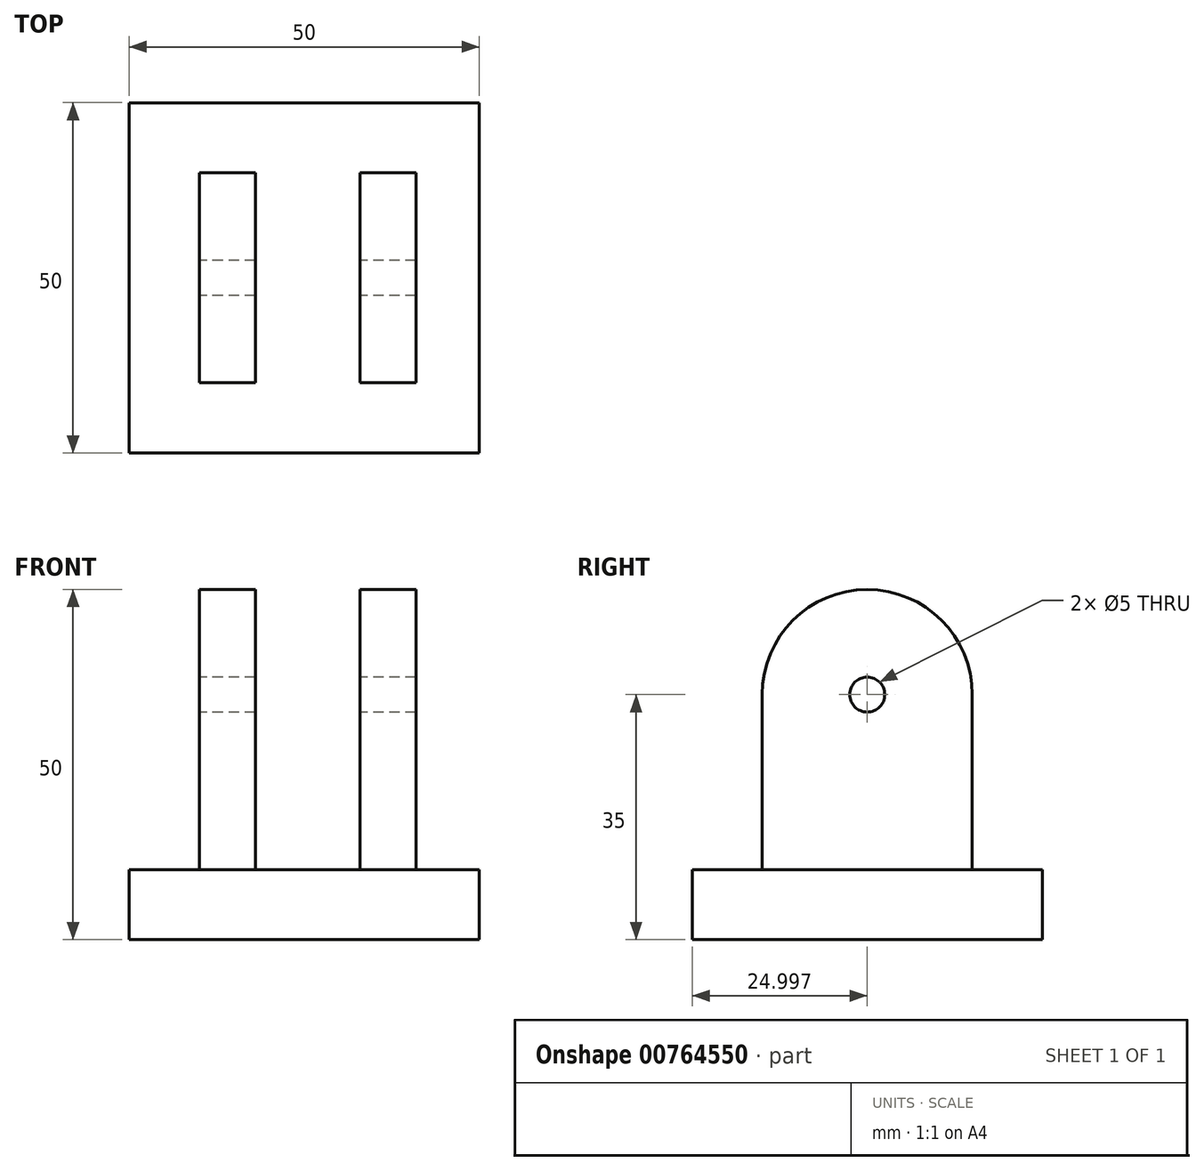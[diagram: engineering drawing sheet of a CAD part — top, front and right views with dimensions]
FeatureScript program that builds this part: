
annotation { "Feature Type Name" : "Feature", "Feature Type Description" : "" }
export const myFeature = defineFeature(function(context is Context, id is Id, definition is map)
    precondition{}
    {
        {
            var Q0;
            Q0=qCreatedBy(makeId("Top.planeOp"),FACE);
            var sketch = newSketch(context, id + "F0", { "sketchPlane" : qUnion([Q0])});
            skLineSegment(sketch, "E0.bottom", {"start": v(-23.15, 24.72) * mm, "end": v(26.85, 24.72) * mm});
            skLineSegment(sketch, "E0.top", {"start": v(-23.15, -25.28) * mm, "end": v(26.85, -25.28) * mm});
            skLineSegment(sketch, "E0.left", {"start": v(-23.15, 24.72) * mm, "end": v(-23.15, -25.28) * mm});
            skLineSegment(sketch, "E0.right", {"start": v(26.85, 24.72) * mm, "end": v(26.85, -25.28) * mm});
            skSolve(sketch);
        }
        {
            var Q0;
            Q0=makeQuery(id+"F0.imprint","IMPRINT",FACE,{"disambiguationData":[TD([[makeQuery(id+"F0.imprint","IMPRINT",EDGE,{"derivedFrom":sQuery(id+"F0.wireOp",EDGE,"E0.bottom")}),-1.0]])]});
            extrude(context, id + "F1", {"entities" : qUnion([Q0]), "depth" : 10 * mm, "offsetDistance" : 25 * mm});
        }
        {
            var Q0;
            Q0=makeQuery(id+"F1.opExtrude","CAP_FACE",FACE,{"disambiguationData":[OSD([sQuery(id+"F0.wireOp",EDGE,"E0.bottom"),sQuery(id+"F0.wireOp",EDGE,"E0.top"),sQuery(id+"F0.wireOp",EDGE,"E0.left"),sQuery(id+"F0.wireOp",EDGE,"E0.right")])],"isStart":false});
            var sketch = newSketch(context, id + "F2", { "sketchPlane" : qUnion([Q0])});
            skLineSegment(sketch, "E1.bottom", {"start": v(-13.15, 14.72) * mm, "end": v(-5.15, 14.72) * mm});
            skLineSegment(sketch, "E1.top", {"start": v(-13.15, -15.28) * mm, "end": v(-5.15, -15.28) * mm});
            skLineSegment(sketch, "E1.left", {"start": v(-13.15, 14.72) * mm, "end": v(-13.15, -15.28) * mm});
            skLineSegment(sketch, "E1.right", {"start": v(-5.15, 14.72) * mm, "end": v(-5.15, -15.28) * mm});
            skSolve(sketch);
        }
        {
            var Q0;
            Q0=makeQuery(id+"F2.imprint","IMPRINT",FACE,{"disambiguationData":[TD([[makeQuery(id+"F2.imprint","IMPRINT",EDGE,{"derivedFrom":sQuery(id+"F2.wireOp",EDGE,"E1.bottom")}),1.0]])]});
            var sketch = newSketch(context, id + "F3", { "sketchPlane" : qUnion([Q0])});
            skLineSegment(sketch, "E2.bottom", {"start": v(9.78, 14.72) * mm, "end": v(17.78, 14.72) * mm});
            skLineSegment(sketch, "E2.top", {"start": v(9.78, -15.28) * mm, "end": v(17.78, -15.28) * mm});
            skLineSegment(sketch, "E2.left", {"start": v(9.78, 14.72) * mm, "end": v(9.78, -15.28) * mm});
            skLineSegment(sketch, "E2.right", {"start": v(17.78, 14.72) * mm, "end": v(17.78, -15.28) * mm});
            skSolve(sketch);
        }
        {
            var Q0;
            Q0=makeQuery(id+"F2.imprint","IMPRINT",FACE,{"disambiguationData":[TD([[makeQuery(id+"F2.imprint","IMPRINT",EDGE,{"derivedFrom":sQuery(id+"F2.wireOp",EDGE,"E1.bottom")}),-1.0]])]});
            extrude(context, id + "F4", {"entities" : qUnion([Q0]), "operationType" : NewBodyOperationType.ADD, "depth" : 40 * mm, "offsetDistance" : 25 * mm});
        }
        {
            var Q0;
            Q0=makeQuery(id+"F3.imprint","IMPRINT",FACE,{"disambiguationData":[TD([[makeQuery(id+"F3.imprint","IMPRINT",EDGE,{"derivedFrom":sQuery(id+"F3.wireOp",EDGE,"E2.bottom")}),-1.0]])]});
            extrude(context, id + "F5", {"entities" : qUnion([Q0]), "operationType" : NewBodyOperationType.ADD, "depth" : 40 * mm, "offsetDistance" : 25 * mm});
        }
        {
            var Q0;
            Q0=makeQuery(id+"F4.opExtrude","CAP_EDGE",EDGE,{"disambiguationData":[OSD([sQuery(id+"F2.wireOp",EDGE,"E1.top")])],"isStart":false});
            var Q1;
            Q1=makeQuery(id+"F5.opExtrude","CAP_EDGE",EDGE,{"disambiguationData":[OSD([sQuery(id+"F3.wireOp",EDGE,"E2.top")])],"isStart":false});
            var Q2;
            Q2=makeQuery(id+"F4.opExtrude","CAP_EDGE",EDGE,{"disambiguationData":[OSD([sQuery(id+"F2.wireOp",EDGE,"E1.bottom")])],"isStart":false});
            var Q3;
            Q3=makeQuery(id+"F5.opExtrude","CAP_EDGE",EDGE,{"disambiguationData":[OSD([sQuery(id+"F3.wireOp",EDGE,"E2.bottom")])],"isStart":false});
            fillet(context, id + "F6", {"entities" : qUnion([Q0, Q1, Q2, Q3]), "radius" : 15 * mm, "tangentPropagation" : true, "allowEdgeOverflow" : false});
        }
        {
            var Q0;
            Q0=makeQuery(id+"F4.opExtrude","SWEPT_FACE",FACE,{"disambiguationData":[OSD([sQuery(id+"F2.wireOp",EDGE,"E1.left")])]});
            var sketch = newSketch(context, id + "F7", { "sketchPlane" : qUnion([Q0])});
            skCircle(sketch, "E3", {"center": v(0.28, 35) * mm, "radius": 2.5 * mm});
            skSolve(sketch);
        }
        {
            var Q0;
            Q0=sQuery(id+"F7.wireOp",VERTEX,"E3.center");
            var Q1;
            Q1=makeQuery(id+"F1.opExtrude","SWEPT_BODY",BODY,{"disambiguationData":[OSD([sQuery(id+"F0.wireOp",EDGE,"E0.bottom"),sQuery(id+"F0.wireOp",EDGE,"E0.top"),sQuery(id+"F0.wireOp",EDGE,"E0.left"),sQuery(id+"F0.wireOp",EDGE,"E0.right")])]});
            hole(context, id + "F8", {"style" : HoleStyle.SIMPLE, "endStyle" : HoleEndStyle.THROUGH, "holeDiameter" : 5 * mm, "majorDiameter" : 5 * mm, "isTappedThrough" : true, "tappedDepth" : 12 * mm, "tapClearance" : 3, "locations" : qUnion([Q0]), "scope" : qUnion([Q1])});
        }
    });
